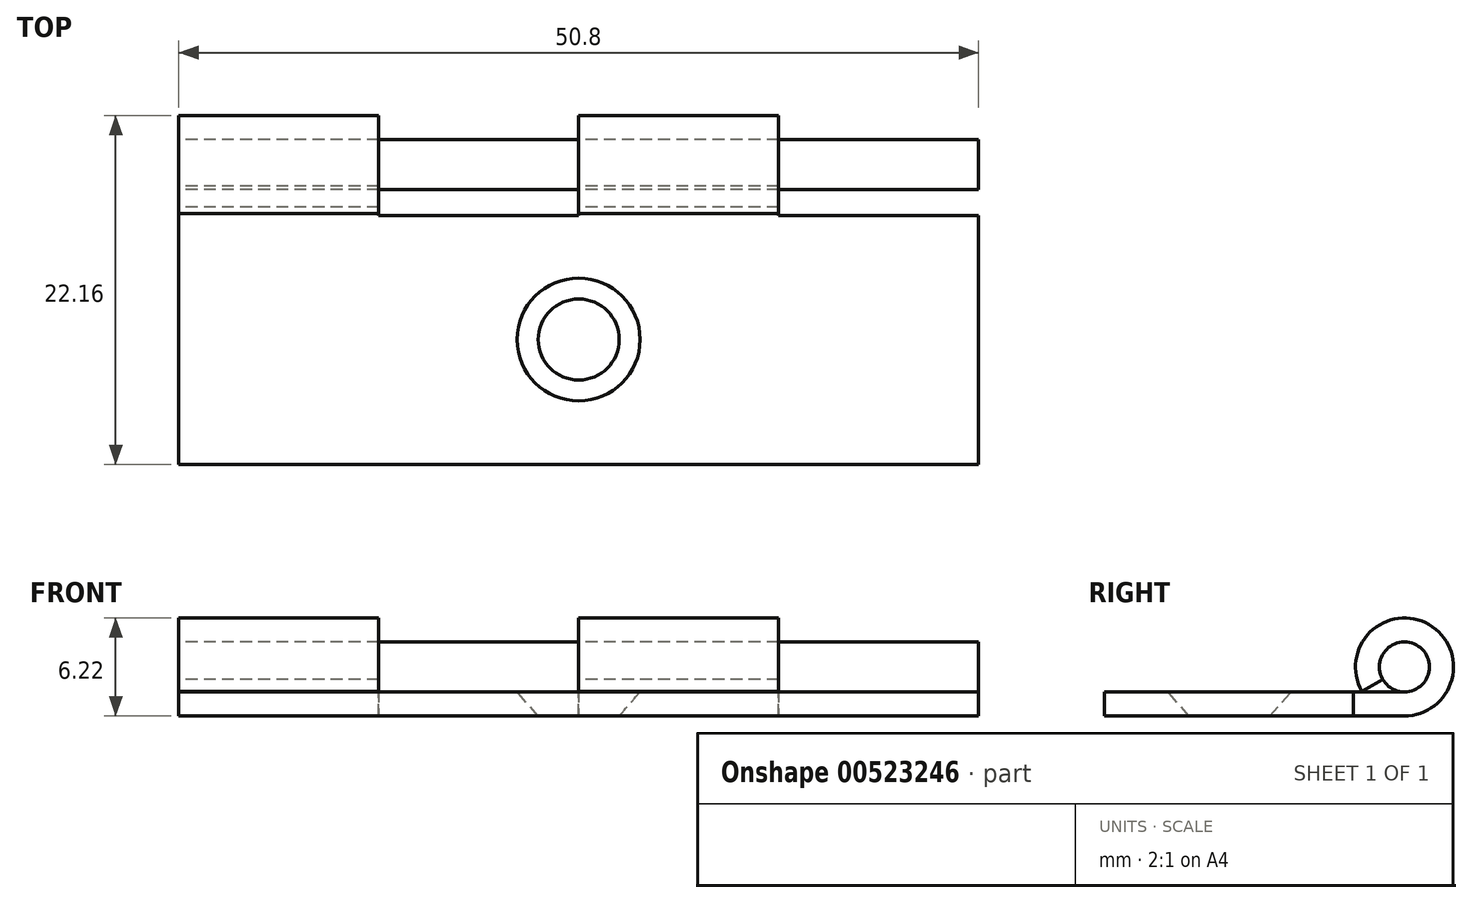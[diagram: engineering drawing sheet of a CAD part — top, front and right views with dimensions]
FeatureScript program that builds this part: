
annotation { "Feature Type Name" : "Feature", "Feature Type Description" : "" }
export const myFeature = defineFeature(function(context is Context, id is Id, definition is map)
    precondition{}
    {
        {
            var Q0;
            Q0=qCreatedBy(makeId("Right.planeOp"),FACE);
            var sketch = newSketch(context, id + "F0", { "sketchPlane" : qUnion([Q0])});
            skArc(sketch, "E0", {"start": v(0, -3.11) * mm, "mid": v(1.56, 2.7) * mm, "end": v(-2.7, -1.54) * mm});
            skLineSegment(sketch, "E1", {"start": v(0, -3.11) * mm, "end": v(-19.05, -3.11) * mm});
            skArc(sketch, "E2", {"start": v(0, -1.59) * mm, "mid": v(0.8, 1.37) * mm, "end": v(-1.38, -0.79) * mm});
            skLineSegment(sketch, "E3", {"start": v(0, -1.59) * mm, "end": v(-19.05, -1.59) * mm});
            skLineSegment(sketch, "E4", {"start": v(-19.05, -3.11) * mm, "end": v(-19.05, -1.59) * mm});
            skLineSegment(sketch, "E5", {"start": v(-2.68, -1.59) * mm, "end": v(-1.37, -0.8) * mm, "construction": true});
            skLineSegment(sketch, "E6", {"start": v(0, 0) * mm, "end": v(0, 10.16) * mm, "construction": true});
            skLineSegment(sketch, "E7", {"start": v(0, 0) * mm, "end": v(-2.7, -1.54) * mm});
            skSolve(sketch);
        }
        {
            var Q0;
            {var subQ2=sQuery(id+"F0.wireOp",EDGE,"E0");Q0=makeQuery(id+"F0.imprint","IMPRINT",FACE,{"disambiguationData":[TD([[makeQuery(id+"F0.imprint","IMPRINT",EDGE,{"derivedFrom":subQ2}),1.0]])]});}
            extrude(context, id + "F1", {"entities" : qUnion([Q0]), "depth" : 50.8 * mm, "offsetDistance" : 25.4 * mm});
        }
        {
            var Q0;
            Q0=qCreatedBy(makeId("Top.planeOp"),FACE);
            var sketch = newSketch(context, id + "F2", { "sketchPlane" : qUnion([Q0])});
            skLineSegment(sketch, "E8.0.0", {"start": v(0, 3.11) * mm, "end": v(0, -3.11) * mm});
            skLineSegment(sketch, "E9", {"start": v(12.7, 3.11) * mm, "end": v(12.7, -3.24) * mm});
            skLineSegment(sketch, "E10", {"start": v(25.4, 3.11) * mm, "end": v(25.4, -3.24) * mm});
            skLineSegment(sketch, "E11", {"start": v(12.7, 3.11) * mm, "end": v(25.4, 3.11) * mm});
            skPoint(sketch, "E12.orphan", {"position": v(0, -2.7) * mm});
            skLineSegment(sketch, "E13", {"start": v(12.7, -3.24) * mm, "end": v(25.4, -3.24) * mm});
            skPoint(sketch, "E14.orphan", {"position": v(39.57, -3.24) * mm});
            skLineSegment(sketch, "E15.1.0.0", {"start": v(50.8, 3.11) * mm, "end": v(50.8, -3.24) * mm});
            skLineSegment(sketch, "E15.1.0.1", {"start": v(38.1, 3.11) * mm, "end": v(38.1, -3.24) * mm});
            skLineSegment(sketch, "E15.1.0.2", {"start": v(38.1, -3.24) * mm, "end": v(50.8, -3.24) * mm});
            skLineSegment(sketch, "E15.1.0.3", {"start": v(38.1, 3.11) * mm, "end": v(50.8, 3.11) * mm});
            skLineSegment(sketch, "E15.2.0.0", {"start": v(76.2, 3.11) * mm, "end": v(76.2, -3.24) * mm});
            skLineSegment(sketch, "E15.2.0.1", {"start": v(63.5, 3.11) * mm, "end": v(63.5, -3.24) * mm});
            skLineSegment(sketch, "E15.2.0.2", {"start": v(63.5, -3.24) * mm, "end": v(76.2, -3.24) * mm});
            skLineSegment(sketch, "E15.2.0.3", {"start": v(63.5, 3.11) * mm, "end": v(76.2, 3.11) * mm});
            skLineSegment(sketch, "E15.3.0.0", {"start": v(101.6, 3.11) * mm, "end": v(101.6, -3.24) * mm});
            skLineSegment(sketch, "E15.3.0.1", {"start": v(88.9, 3.11) * mm, "end": v(88.9, -3.24) * mm});
            skLineSegment(sketch, "E15.3.0.2", {"start": v(88.9, -3.24) * mm, "end": v(101.6, -3.24) * mm});
            skLineSegment(sketch, "E15.3.0.3", {"start": v(88.9, 3.11) * mm, "end": v(101.6, 3.11) * mm});
            skLineSegment(sketch, "E15.4.0.0", {"start": v(127, 3.11) * mm, "end": v(127, -3.24) * mm});
            skLineSegment(sketch, "E15.4.0.1", {"start": v(114.3, 3.11) * mm, "end": v(114.3, -3.24) * mm});
            skLineSegment(sketch, "E15.4.0.2", {"start": v(114.3, -3.24) * mm, "end": v(127, -3.24) * mm});
            skLineSegment(sketch, "E15.4.0.3", {"start": v(114.3, 3.11) * mm, "end": v(127, 3.11) * mm});
            skLineSegment(sketch, "E15.5.0.0", {"start": v(152.4, 3.11) * mm, "end": v(152.4, -3.24) * mm});
            skLineSegment(sketch, "E15.5.0.1", {"start": v(139.7, 3.11) * mm, "end": v(139.7, -3.24) * mm});
            skLineSegment(sketch, "E15.5.0.2", {"start": v(139.7, -3.24) * mm, "end": v(152.4, -3.24) * mm});
            skLineSegment(sketch, "E15.5.0.3", {"start": v(139.7, 3.11) * mm, "end": v(152.4, 3.11) * mm});
            skLineSegment(sketch, "E15.6.0.0", {"start": v(177.8, 3.11) * mm, "end": v(177.8, -3.24) * mm});
            skLineSegment(sketch, "E15.6.0.1", {"start": v(165.1, 3.11) * mm, "end": v(165.1, -3.24) * mm});
            skLineSegment(sketch, "E15.6.0.2", {"start": v(165.1, -3.24) * mm, "end": v(177.8, -3.24) * mm});
            skLineSegment(sketch, "E15.6.0.3", {"start": v(165.1, 3.11) * mm, "end": v(177.8, 3.11) * mm});
            skLineSegment(sketch, "E15.7.0.0", {"start": v(203.2, 3.11) * mm, "end": v(203.2, -3.24) * mm});
            skLineSegment(sketch, "E15.7.0.1", {"start": v(190.5, 3.11) * mm, "end": v(190.5, -3.24) * mm});
            skLineSegment(sketch, "E15.7.0.2", {"start": v(190.5, -3.24) * mm, "end": v(203.2, -3.24) * mm});
            skLineSegment(sketch, "E15.7.0.3", {"start": v(190.5, 3.11) * mm, "end": v(203.2, 3.11) * mm});
            skLineSegment(sketch, "E15.8.0.0", {"start": v(228.6, 3.11) * mm, "end": v(228.6, -3.24) * mm});
            skLineSegment(sketch, "E15.8.0.1", {"start": v(215.9, 3.11) * mm, "end": v(215.9, -3.24) * mm});
            skLineSegment(sketch, "E15.8.0.2", {"start": v(215.9, -3.24) * mm, "end": v(228.6, -3.24) * mm});
            skLineSegment(sketch, "E15.8.0.3", {"start": v(215.9, 3.11) * mm, "end": v(228.6, 3.11) * mm});
            skLineSegment(sketch, "E15.9.0.0", {"start": v(254, 3.11) * mm, "end": v(254, -3.24) * mm});
            skLineSegment(sketch, "E15.9.0.1", {"start": v(241.3, 3.11) * mm, "end": v(241.3, -3.24) * mm});
            skLineSegment(sketch, "E15.9.0.2", {"start": v(241.3, -3.24) * mm, "end": v(254, -3.24) * mm});
            skLineSegment(sketch, "E15.9.0.3", {"start": v(241.3, 3.11) * mm, "end": v(254, 3.11) * mm});
            skLineSegment(sketch, "E15.10.0.0", {"start": v(279.4, 3.11) * mm, "end": v(279.4, -3.24) * mm});
            skLineSegment(sketch, "E15.10.0.1", {"start": v(266.7, 3.11) * mm, "end": v(266.7, -3.24) * mm});
            skLineSegment(sketch, "E15.10.0.2", {"start": v(266.7, -3.24) * mm, "end": v(279.4, -3.24) * mm});
            skLineSegment(sketch, "E15.10.0.3", {"start": v(266.7, 3.11) * mm, "end": v(279.4, 3.11) * mm});
            skLineSegment(sketch, "E15.11.0.0", {"start": v(304.8, 3.11) * mm, "end": v(304.8, -3.24) * mm});
            skLineSegment(sketch, "E15.11.0.1", {"start": v(292.1, 3.11) * mm, "end": v(292.1, -3.24) * mm});
            skLineSegment(sketch, "E15.11.0.2", {"start": v(292.1, -3.24) * mm, "end": v(304.8, -3.24) * mm});
            skLineSegment(sketch, "E15.11.0.3", {"start": v(292.1, 3.11) * mm, "end": v(304.8, 3.11) * mm});
            skLineSegment(sketch, "E15.12.0.0", {"start": v(330.2, 3.11) * mm, "end": v(330.2, -3.24) * mm});
            skLineSegment(sketch, "E15.12.0.1", {"start": v(317.5, 3.11) * mm, "end": v(317.5, -3.24) * mm});
            skLineSegment(sketch, "E15.12.0.2", {"start": v(317.5, -3.24) * mm, "end": v(330.2, -3.24) * mm});
            skLineSegment(sketch, "E15.12.0.3", {"start": v(317.5, 3.11) * mm, "end": v(330.2, 3.11) * mm});
            skLineSegment(sketch, "E15.13.0.0", {"start": v(355.6, 3.11) * mm, "end": v(355.6, -3.24) * mm});
            skLineSegment(sketch, "E15.13.0.1", {"start": v(342.9, 3.11) * mm, "end": v(342.9, -3.24) * mm});
            skLineSegment(sketch, "E15.13.0.2", {"start": v(342.9, -3.24) * mm, "end": v(355.6, -3.24) * mm});
            skLineSegment(sketch, "E15.13.0.3", {"start": v(342.9, 3.11) * mm, "end": v(355.6, 3.11) * mm});
            skLineSegment(sketch, "E15.14.0.0", {"start": v(381, 3.11) * mm, "end": v(381, -3.24) * mm});
            skLineSegment(sketch, "E15.14.0.1", {"start": v(368.3, 3.11) * mm, "end": v(368.3, -3.24) * mm});
            skLineSegment(sketch, "E15.14.0.2", {"start": v(368.3, -3.24) * mm, "end": v(381, -3.24) * mm});
            skLineSegment(sketch, "E15.14.0.3", {"start": v(368.3, 3.11) * mm, "end": v(381, 3.11) * mm});
            skLineSegment(sketch, "E15.15.0.0", {"start": v(406.4, 3.11) * mm, "end": v(406.4, -3.24) * mm});
            skLineSegment(sketch, "E15.15.0.1", {"start": v(393.7, 3.11) * mm, "end": v(393.7, -3.24) * mm});
            skLineSegment(sketch, "E15.15.0.2", {"start": v(393.7, -3.24) * mm, "end": v(406.4, -3.24) * mm});
            skLineSegment(sketch, "E15.15.0.3", {"start": v(393.7, 3.11) * mm, "end": v(406.4, 3.11) * mm});
            skLineSegment(sketch, "E15.16.0.0", {"start": v(431.8, 3.11) * mm, "end": v(431.8, -3.24) * mm});
            skLineSegment(sketch, "E15.16.0.1", {"start": v(419.1, 3.11) * mm, "end": v(419.1, -3.24) * mm});
            skLineSegment(sketch, "E15.16.0.2", {"start": v(419.1, -3.24) * mm, "end": v(431.8, -3.24) * mm});
            skLineSegment(sketch, "E15.16.0.3", {"start": v(419.1, 3.11) * mm, "end": v(431.8, 3.11) * mm});
            skLineSegment(sketch, "E15.17.0.0", {"start": v(457.2, 3.11) * mm, "end": v(457.2, -3.24) * mm});
            skLineSegment(sketch, "E15.17.0.1", {"start": v(444.5, 3.11) * mm, "end": v(444.5, -3.24) * mm});
            skLineSegment(sketch, "E15.17.0.2", {"start": v(444.5, -3.24) * mm, "end": v(457.2, -3.24) * mm});
            skLineSegment(sketch, "E15.17.0.3", {"start": v(444.5, 3.11) * mm, "end": v(457.2, 3.11) * mm});
            skLineSegment(sketch, "E15.18.0.0", {"start": v(482.6, 3.11) * mm, "end": v(482.6, -3.24) * mm});
            skLineSegment(sketch, "E15.18.0.1", {"start": v(469.9, 3.11) * mm, "end": v(469.9, -3.24) * mm});
            skLineSegment(sketch, "E15.18.0.2", {"start": v(469.9, -3.24) * mm, "end": v(482.6, -3.24) * mm});
            skLineSegment(sketch, "E15.18.0.3", {"start": v(469.9, 3.11) * mm, "end": v(482.6, 3.11) * mm});
            skLineSegment(sketch, "E15.19.0.0", {"start": v(508, 3.11) * mm, "end": v(508, -3.24) * mm});
            skLineSegment(sketch, "E15.19.0.1", {"start": v(495.3, 3.11) * mm, "end": v(495.3, -3.24) * mm});
            skLineSegment(sketch, "E15.19.0.2", {"start": v(495.3, -3.24) * mm, "end": v(508, -3.24) * mm});
            skLineSegment(sketch, "E15.19.0.3", {"start": v(495.3, 3.11) * mm, "end": v(508, 3.11) * mm});
            skLineSegment(sketch, "E15.20.0.0", {"start": v(533.4, 3.11) * mm, "end": v(533.4, -3.24) * mm});
            skLineSegment(sketch, "E15.20.0.1", {"start": v(520.7, 3.11) * mm, "end": v(520.7, -3.24) * mm});
            skLineSegment(sketch, "E15.20.0.2", {"start": v(520.7, -3.24) * mm, "end": v(533.4, -3.24) * mm});
            skLineSegment(sketch, "E15.20.0.3", {"start": v(520.7, 3.11) * mm, "end": v(533.4, 3.11) * mm});
            skLineSegment(sketch, "E15.21.0.0", {"start": v(558.8, 3.11) * mm, "end": v(558.8, -3.24) * mm});
            skLineSegment(sketch, "E15.21.0.1", {"start": v(546.1, 3.11) * mm, "end": v(546.1, -3.24) * mm});
            skLineSegment(sketch, "E15.21.0.2", {"start": v(546.1, -3.24) * mm, "end": v(558.8, -3.24) * mm});
            skLineSegment(sketch, "E15.21.0.3", {"start": v(546.1, 3.11) * mm, "end": v(558.8, 3.11) * mm});
            skLineSegment(sketch, "E15.22.0.0", {"start": v(584.2, 3.11) * mm, "end": v(584.2, -3.24) * mm});
            skLineSegment(sketch, "E15.22.0.1", {"start": v(571.5, 3.11) * mm, "end": v(571.5, -3.24) * mm});
            skLineSegment(sketch, "E15.22.0.2", {"start": v(571.5, -3.24) * mm, "end": v(584.2, -3.24) * mm});
            skLineSegment(sketch, "E15.22.0.3", {"start": v(571.5, 3.11) * mm, "end": v(584.2, 3.11) * mm});
            skLineSegment(sketch, "E15.23.0.0", {"start": v(609.6, 3.11) * mm, "end": v(609.6, -3.24) * mm});
            skLineSegment(sketch, "E15.23.0.1", {"start": v(596.9, 3.11) * mm, "end": v(596.9, -3.24) * mm});
            skLineSegment(sketch, "E15.23.0.2", {"start": v(596.9, -3.24) * mm, "end": v(609.6, -3.24) * mm});
            skLineSegment(sketch, "E15.23.0.3", {"start": v(596.9, 3.11) * mm, "end": v(609.6, 3.11) * mm});
            skLineSegment(sketch, "E15.24.0.0", {"start": v(635, 3.11) * mm, "end": v(635, -3.24) * mm});
            skLineSegment(sketch, "E15.24.0.1", {"start": v(622.3, 3.11) * mm, "end": v(622.3, -3.24) * mm});
            skLineSegment(sketch, "E15.24.0.2", {"start": v(622.3, -3.24) * mm, "end": v(635, -3.24) * mm});
            skLineSegment(sketch, "E15.24.0.3", {"start": v(622.3, 3.11) * mm, "end": v(635, 3.11) * mm});
            skLineSegment(sketch, "E15.25.0.0", {"start": v(660.4, 3.11) * mm, "end": v(660.4, -3.24) * mm});
            skLineSegment(sketch, "E15.25.0.1", {"start": v(647.7, 3.11) * mm, "end": v(647.7, -3.24) * mm});
            skLineSegment(sketch, "E15.25.0.2", {"start": v(647.7, -3.24) * mm, "end": v(660.4, -3.24) * mm});
            skLineSegment(sketch, "E15.25.0.3", {"start": v(647.7, 3.11) * mm, "end": v(660.4, 3.11) * mm});
            skLineSegment(sketch, "E15.26.0.0", {"start": v(685.8, 3.11) * mm, "end": v(685.8, -3.24) * mm});
            skLineSegment(sketch, "E15.26.0.1", {"start": v(673.1, 3.11) * mm, "end": v(673.1, -3.24) * mm});
            skLineSegment(sketch, "E15.26.0.2", {"start": v(673.1, -3.24) * mm, "end": v(685.8, -3.24) * mm});
            skLineSegment(sketch, "E15.26.0.3", {"start": v(673.1, 3.11) * mm, "end": v(685.8, 3.11) * mm});
            skLineSegment(sketch, "E15.27.0.0", {"start": v(711.2, 3.11) * mm, "end": v(711.2, -3.24) * mm});
            skLineSegment(sketch, "E15.27.0.1", {"start": v(698.5, 3.11) * mm, "end": v(698.5, -3.24) * mm});
            skLineSegment(sketch, "E15.27.0.2", {"start": v(698.5, -3.24) * mm, "end": v(711.2, -3.24) * mm});
            skLineSegment(sketch, "E15.27.0.3", {"start": v(698.5, 3.11) * mm, "end": v(711.2, 3.11) * mm});
            skLineSegment(sketch, "E15.28.0.0", {"start": v(736.6, 3.11) * mm, "end": v(736.6, -3.24) * mm});
            skLineSegment(sketch, "E15.28.0.1", {"start": v(723.9, 3.11) * mm, "end": v(723.9, -3.24) * mm});
            skLineSegment(sketch, "E15.28.0.2", {"start": v(723.9, -3.24) * mm, "end": v(736.6, -3.24) * mm});
            skLineSegment(sketch, "E15.28.0.3", {"start": v(723.9, 3.11) * mm, "end": v(736.6, 3.11) * mm});
            skLineSegment(sketch, "E15.29.0.0", {"start": v(762, 3.11) * mm, "end": v(762, -3.24) * mm});
            skLineSegment(sketch, "E15.29.0.1", {"start": v(749.3, 3.11) * mm, "end": v(749.3, -3.24) * mm});
            skLineSegment(sketch, "E15.29.0.2", {"start": v(749.3, -3.24) * mm, "end": v(762, -3.24) * mm});
            skLineSegment(sketch, "E15.29.0.3", {"start": v(749.3, 3.11) * mm, "end": v(762, 3.11) * mm});
            skLineSegment(sketch, "E15.direction1", {"start": v(12.7, -3.24) * mm, "end": v(38.1, -3.24) * mm, "construction": true});
            skSolve(sketch);
        }
        {
            var Q0;
            Q0=qSketchRegion(id+"F2",true);
            extrude(context, id + "F3", {"entities" : qUnion([Q0]), "operationType" : NewBodyOperationType.REMOVE, "endBound" : BoundingType.THROUGH_ALL, "oppositeDirection" : true, "depth" : 25.4 * mm, "hasSecondDirection" : true, "secondDirectionBound" : BoundingType.THROUGH_ALL, "secondDirectionOppositeDirection" : false, "secondDirectionDepth" : 25.4 * mm});
        }
        {
            var Q0;
            Q0=makeQuery(id+"F1.opExtrude","SWEPT_FACE",FACE,{"disambiguationData":[OSD([sQuery(id+"F0.wireOp",EDGE,"E3")])]});
            var sketch = newSketch(context, id + "F4", { "sketchPlane" : qUnion([Q0])});
            skPoint(sketch, "E16", {"position": v(25.4, -11.11) * mm});
            skSolve(sketch);
        }
        {
            var Q0;
            Q0=sQuery(id+"F4.wireOp",VERTEX,"E16");
            var Q1;
            Q1=makeQuery(id+"F1.opExtrude","SWEPT_BODY",BODY,{"disambiguationData":[OSD([sQuery(id+"F0.wireOp",EDGE,"E0"),sQuery(id+"F0.wireOp",EDGE,"E1"),sQuery(id+"F0.wireOp",EDGE,"E2"),sQuery(id+"F0.wireOp",EDGE,"E3"),sQuery(id+"F0.wireOp",EDGE,"E4"),sQuery(id+"F0.wireOp",EDGE,"E7")])]});
            hole(context, id + "F5", {"style" : HoleStyle.C_SINK, "endStyle" : HoleEndStyle.THROUGH, "standardTappedOrClearance" : lookupTablePath({ "standard" : "ANSI", "fit" : "Close", "size" : "#6", "type" : "Clearance" }), "standardBlindInLast" : lookupTablePath({ "fit" : "Close", "standard" : "ANSI", "size" : "#6", "type" : "Clearance" }), "holeDiameter" : 3.66 * mm, "cSinkDiameter" : 7.8 * mm, "cSinkAngle" : 82 * degree, "tappedDepth" : 12.7 * mm, "tapClearance" : 3, "startFromSketch" : true, "locations" : qUnion([Q0]), "scope" : qUnion([Q1])});
        }
        {
            var Q0;
            Q0=qCreatedBy(makeId("Right.planeOp"),FACE);
            var sketch = newSketch(context, id + "F6", { "sketchPlane" : qUnion([Q0])});
            skCircle(sketch, "E17", {"center": v(0, 0) * mm, "radius": 1.59 * mm});
            skSolve(sketch);
        }
        {
            var Q0;
            Q0=qSketchRegion(id+"F6",true);
            var Q1;
            Q1=makeQuery(id+"F1.opExtrude","CAP_FACE",FACE,{"disambiguationData":[OSD([sQuery(id+"F0.wireOp",EDGE,"E0"),sQuery(id+"F0.wireOp",EDGE,"E1"),sQuery(id+"F0.wireOp",EDGE,"E2"),sQuery(id+"F0.wireOp",EDGE,"E3"),sQuery(id+"F0.wireOp",EDGE,"E4"),sQuery(id+"F0.wireOp",EDGE,"E7")])],"isStart":false});
            extrude(context, id + "F7", {"entities" : qUnion([Q0]), "endBound" : BoundingType.UP_TO_SURFACE, "endBoundEntityFace" : qUnion([Q1]), "depth" : 762 * mm});
        }
    });
